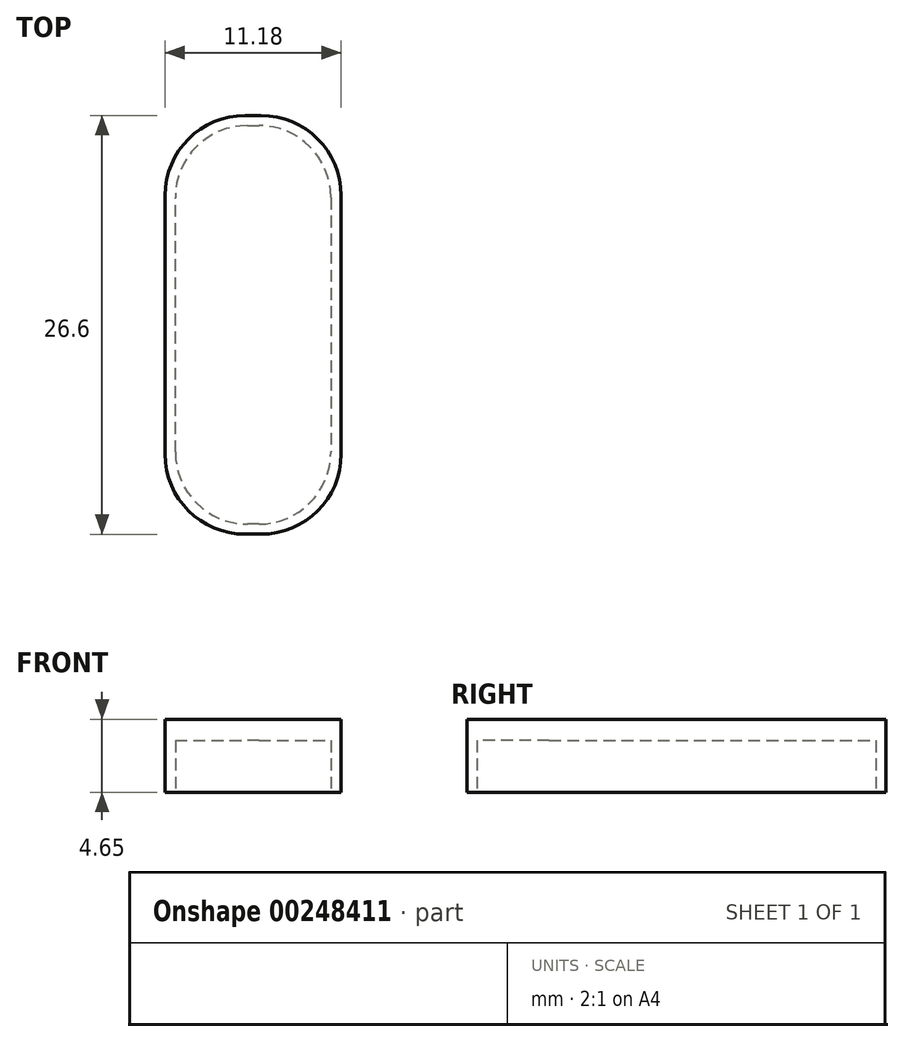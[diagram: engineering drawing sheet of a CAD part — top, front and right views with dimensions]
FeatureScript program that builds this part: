
annotation { "Feature Type Name" : "Feature", "Feature Type Description" : "" }
export const myFeature = defineFeature(function(context is Context, id is Id, definition is map)
    precondition{}
    {
        {
            var Q0;
            Q0=qCreatedBy(makeId("Top.planeOp"),FACE);
            var sketch = newSketch(context, id + "F0", { "sketchPlane" : qUnion([Q0])});
            skLineSegment(sketch, "E0", {"start": v(5.59, 13.3) * mm, "end": v(5.59, -13.3) * mm});
            skLineSegment(sketch, "E1.MirrorCS", {"start": v(-5.59, 13.3) * mm, "end": v(-5.59, -13.3) * mm});
            skLineSegment(sketch, "E2", {"start": v(-5.59, 13.3) * mm, "end": v(5.59, 13.3) * mm});
            skLineSegment(sketch, "E3", {"start": v(5.59, -13.3) * mm, "end": v(-5.59, -13.3) * mm});
            skPoint(sketch, "E4.endSnap0", {"position": v(5.59, 0) * mm});
            skLineSegment(sketch, "E5", {"start": v(-26.29, -22.57) * mm, "end": v(-15.64, -22.57) * mm});
            skLineSegment(sketch, "E6", {"start": v(-15.64, -22.57) * mm, "end": v(-15.64, 3.5) * mm});
            skLineSegment(sketch, "E7", {"start": v(-15.64, 3.5) * mm, "end": v(-26.29, 3.5) * mm});
            skLineSegment(sketch, "E8", {"start": v(-26.29, 3.5) * mm, "end": v(-26.29, -22.57) * mm});
            skLineSegment(sketch, "E9", {"start": v(-7.7, -15.68) * mm, "end": v(-7.7, 15.68) * mm});
            skLineSegment(sketch, "E10", {"start": v(-7.7, 15.68) * mm, "end": v(7.7, 15.68) * mm});
            skLineSegment(sketch, "E11", {"start": v(7.7, 15.68) * mm, "end": v(7.7, -15.68) * mm});
            skLineSegment(sketch, "E12", {"start": v(7.7, -15.68) * mm, "end": v(-7.7, -15.68) * mm});
            skSolve(sketch);
        }
        {
            var Q0;
            Q0=makeQuery(id+"F0.imprint","IMPRINT",FACE,{"disambiguationData":[TD([[makeQuery(id+"F0.imprint","IMPRINT",EDGE,{"derivedFrom":sQuery(id+"F0.wireOp",EDGE,"E0")}),-1.0]])]});
            extrude(context, id + "F1", {"entities" : qUnion([Q0]), "depth" : 4.65 * mm});
        }
        {
            var Q0;
            Q0=makeQuery(id+"F1.opExtrude","SWEPT_EDGE",EDGE,{"disambiguationData":[OSD([sQuery(id+"F0.wireOp",EDGE,"E1.MirrorCS"),sQuery(id+"F0.wireOp",EDGE,"E2")])]});
            var Q1;
            Q1=makeQuery(id+"F1.opExtrude","SWEPT_EDGE",EDGE,{"disambiguationData":[OSD([sQuery(id+"F0.wireOp",EDGE,"E0"),sQuery(id+"F0.wireOp",EDGE,"E2")])]});
            var Q2;
            Q2=makeQuery(id+"F1.opExtrude","SWEPT_EDGE",EDGE,{"disambiguationData":[OSD([sQuery(id+"F0.wireOp",EDGE,"E1.MirrorCS"),sQuery(id+"F0.wireOp",EDGE,"E3")])]});
            var Q3;
            Q3=makeQuery(id+"F1.opExtrude","SWEPT_EDGE",EDGE,{"disambiguationData":[OSD([sQuery(id+"F0.wireOp",EDGE,"E0"),sQuery(id+"F0.wireOp",EDGE,"E3")])]});
            fillet(context, id + "F2", {"entities" : qUnion([Q0, Q1, Q2, Q3]), "radius" : 5.08 * mm, "tangentPropagation" : true, "allowEdgeOverflow" : false});
        }
        {
            var Q0;
            Q0=makeQuery(id+"F0.imprint","IMPRINT",FACE,{"disambiguationData":[TD([[makeQuery(id+"F0.imprint","IMPRINT",EDGE,{"derivedFrom":sQuery(id+"F0.wireOp",EDGE,"E0")}),-1.0]])]});
            var sketch = newSketch(context, id + "F3", { "sketchPlane" : qUnion([Q0])});
            skPoint(sketch, "E13.visualSharp", {"position": v(5.32, 13.04) * mm});
            skPoint(sketch, "E14.visualSharp", {"position": v(-5.32, 13.04) * mm});
            skPoint(sketch, "E15.visualSharp", {"position": v(5.32, -13.04) * mm});
            skPoint(sketch, "E16.visualSharp", {"position": v(-5.32, -13.04) * mm});
            skLineSegment(sketch, "E17", {"start": v(-4.94, -8.09) * mm, "end": v(-4.94, 8.09) * mm});
            skLineSegment(sketch, "E18", {"start": v(-0.37, 12.66) * mm, "end": v(0.37, 12.66) * mm});
            skLineSegment(sketch, "E19", {"start": v(4.94, 8.09) * mm, "end": v(4.94, -8.09) * mm});
            skLineSegment(sketch, "E20", {"start": v(0.37, -12.66) * mm, "end": v(-0.37, -12.66) * mm});
            skPoint(sketch, "E21.visualSharp", {"position": v(-4.94, -12.66) * mm});
            skArc(sketch, "E21.filletArc", {"start": v(-4.94, -8.09) * mm, "mid": v(-3.6, -11.32) * mm, "end": v(-0.37, -12.66) * mm});
            skPoint(sketch, "E22.visualSharp", {"position": v(4.94, -12.66) * mm});
            skArc(sketch, "E22.filletArc", {"start": v(0.37, -12.66) * mm, "mid": v(3.6, -11.32) * mm, "end": v(4.94, -8.09) * mm});
            skPoint(sketch, "E23.visualSharp", {"position": v(-4.94, 12.66) * mm});
            skArc(sketch, "E23.filletArc", {"start": v(-0.37, 12.66) * mm, "mid": v(-3.6, 11.32) * mm, "end": v(-4.94, 8.09) * mm});
            skPoint(sketch, "E24.visualSharp", {"position": v(4.94, 12.66) * mm});
            skArc(sketch, "E24.filletArc", {"start": v(4.94, 8.09) * mm, "mid": v(3.6, 11.32) * mm, "end": v(0.37, 12.66) * mm});
            skSolve(sketch);
        }
        {
            var Q0;
            Q0 = qSketchRegion(id + "F3", true);
            extrude(context, id + "F4", {"entities" : qUnion([Q0]), "operationType" : NewBodyOperationType.REMOVE, "depth" : 3.3 * mm});
        }
    });
